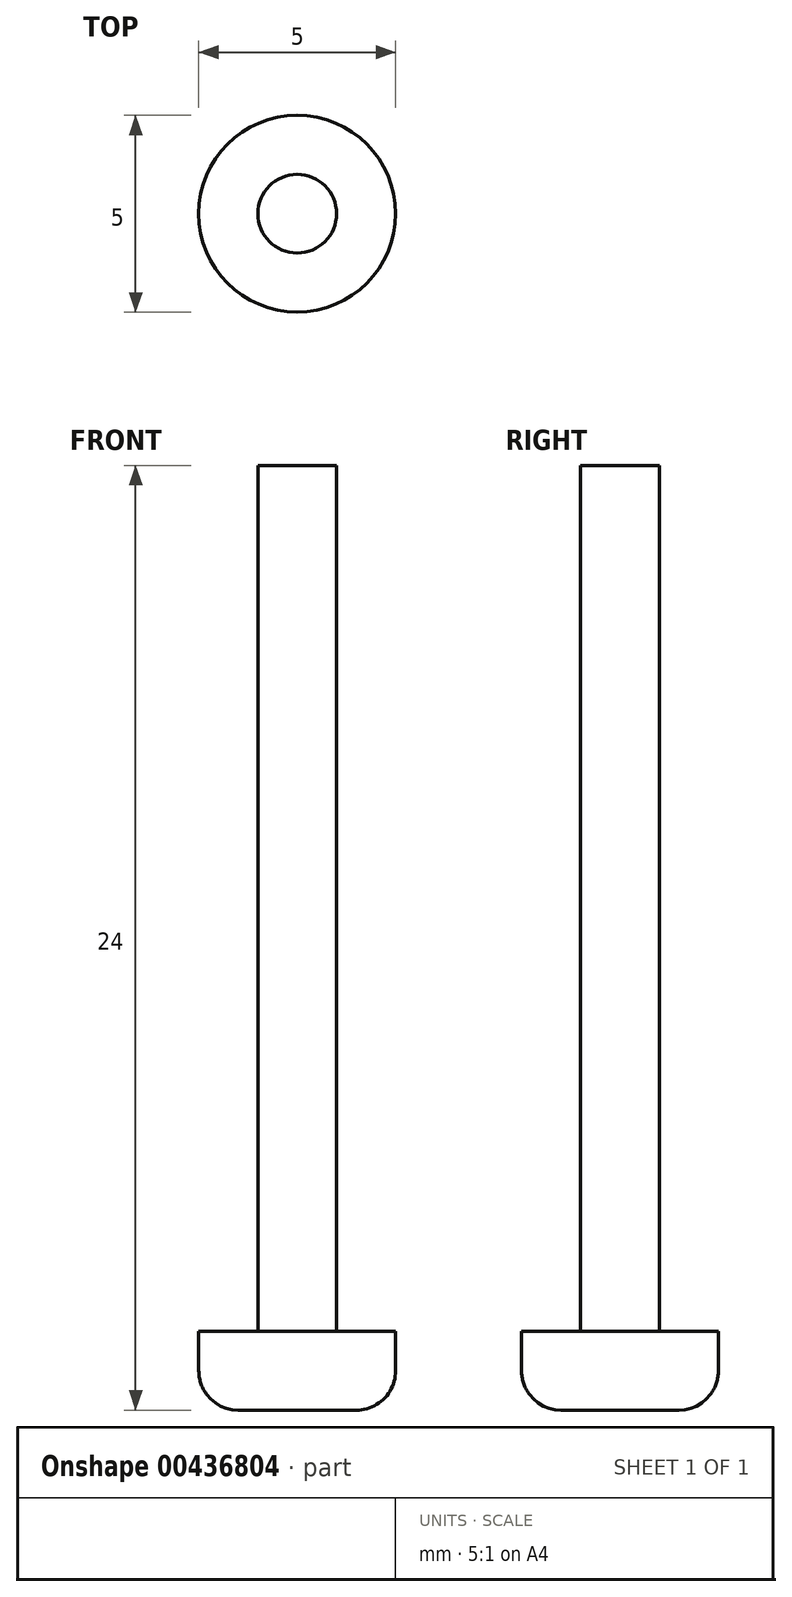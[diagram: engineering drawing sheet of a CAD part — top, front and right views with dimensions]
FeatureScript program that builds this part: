
annotation { "Feature Type Name" : "Feature", "Feature Type Description" : "" }
export const myFeature = defineFeature(function(context is Context, id is Id, definition is map)
    precondition{}
    {
        {
            var Q0;
            Q0=qCreatedBy(makeId("Top.planeOp"),FACE);
            var sketch = newSketch(context, id + "F0", { "sketchPlane" : qUnion([Q0])});
            skCircle(sketch, "E0", {"center": v(0, 0) * mm, "radius": 2.5 * mm});
            skSolve(sketch);
        }
        {
            var Q0;
            Q0 = qSketchRegion(id + "F0", true);
            extrude(context, id + "F1", {"entities" : qUnion([Q0]), "depth" : 2 * mm});
        }
        {
            var Q0;
            Q0=makeQuery(id+"F1.opExtrude","CAP_FACE",FACE,{"disambiguationData":[OSD([sQuery(id+"F0.wireOp",EDGE,"E0")])],"isStart":false});
            var sketch = newSketch(context, id + "F2", { "sketchPlane" : qUnion([Q0])});
            skCircle(sketch, "E1", {"center": v(0, 0) * mm, "radius": 1 * mm});
            skSolve(sketch);
        }
        {
            var Q0;
            Q0 = qSketchRegion(id + "F2", true);
            extrude(context, id + "F3", {"entities" : qUnion([Q0]), "operationType" : NewBodyOperationType.ADD, "depth" : 22 * mm});
        }
        {
            var Q0;
            Q0=makeQuery(id+"F1.opExtrude","CAP_EDGE",EDGE,{"disambiguationData":[OSD([sQuery(id+"F0.wireOp",EDGE,"E0")])],"isStart":true});
            fillet(context, id + "F4", {"entities" : qUnion([Q0]), "radius" : 1 * mm, "tangentPropagation" : true, "allowEdgeOverflow" : false});
        }
    });
